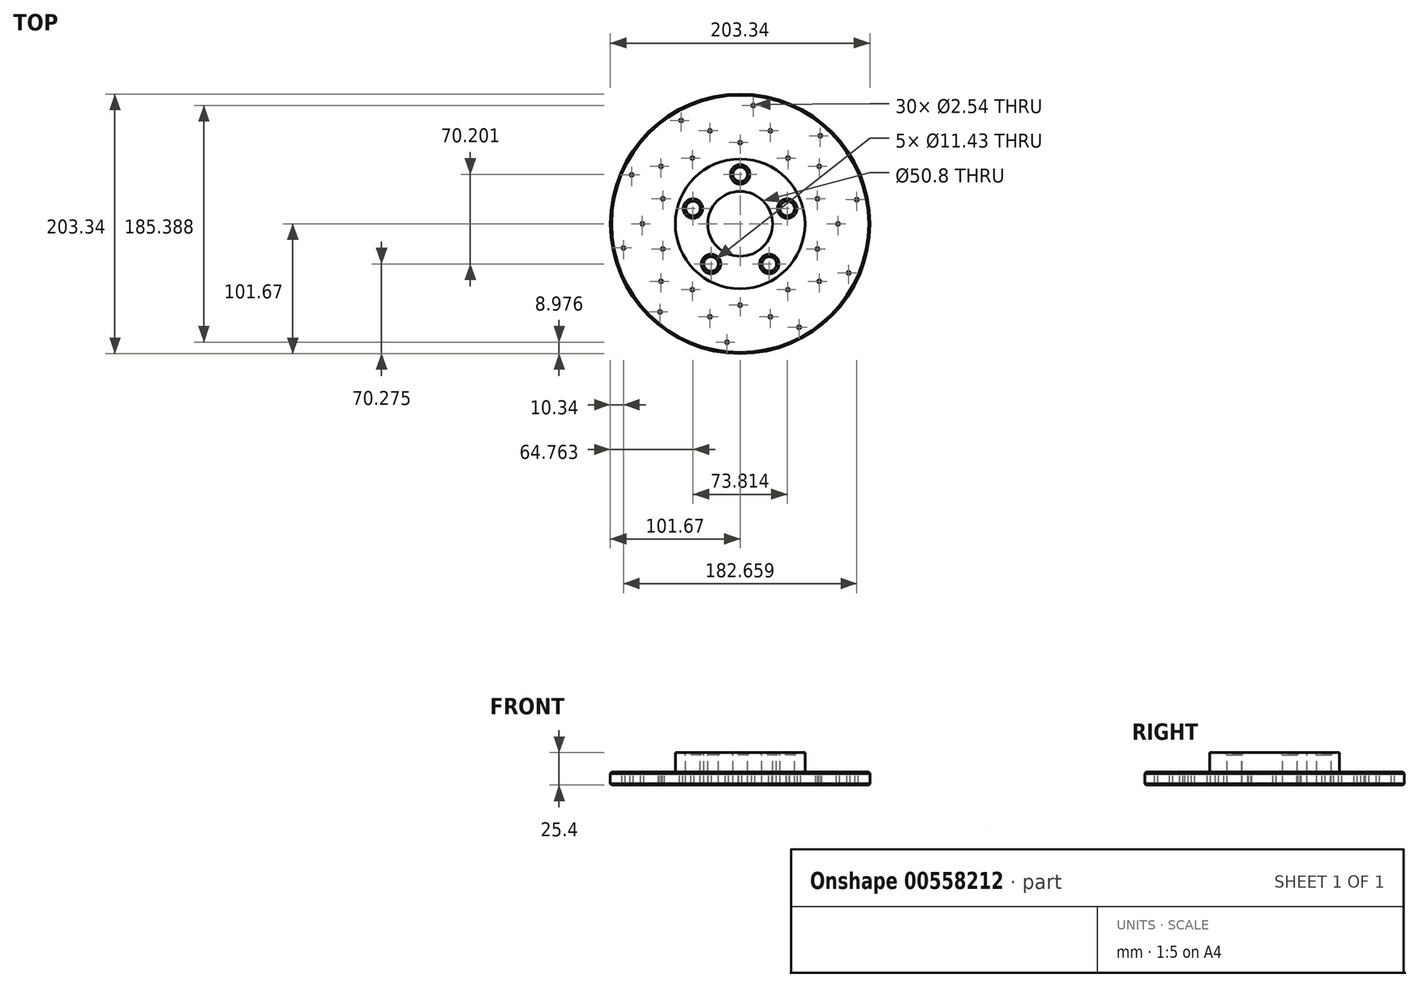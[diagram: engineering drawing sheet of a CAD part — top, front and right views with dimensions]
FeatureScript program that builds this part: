
annotation { "Feature Type Name" : "Feature", "Feature Type Description" : "" }
export const myFeature = defineFeature(function(context is Context, id is Id, definition is map)
    precondition{}
    {
        {
            var Q0;
            Q0=qCreatedBy(makeId("Top.planeOp"),FACE);
            var sketch = newSketch(context, id + "F0", { "sketchPlane" : qUnion([Q0])});
            skCircle(sketch, "E0", {"center": v(0, 0) * mm, "radius": 101.67 * mm});
            skSolve(sketch);
        }
        {
            var Q0;
            Q0=makeQuery(id+"F0.imprint","IMPRINT",FACE,{"disambiguationData":[TD([[makeQuery(id+"F0.imprint","IMPRINT",EDGE,{"derivedFrom":sQuery(id+"F0.wireOp",EDGE,"E0")}),1.0]])]});
            extrude(context, id + "F1", {"entities" : qUnion([Q0]), "depth" : 10.16 * mm, "offsetDistance" : 25.4 * mm});
        }
        {
            var Q0;
            Q0=makeQuery(id+"F1.opExtrude","CAP_FACE",FACE,{"disambiguationData":[OSD([sQuery(id+"F0.wireOp",EDGE,"E0")])],"isStart":false});
            var sketch = newSketch(context, id + "F2", { "sketchPlane" : qUnion([Q0])});
            skCircle(sketch, "E1", {"center": v(0, 0) * mm, "radius": 50.83 * mm});
            skSolve(sketch);
        }
        {
            var Q0;
            Q0=makeQuery(id+"F2.imprint","IMPRINT",FACE,{"disambiguationData":[TD([[makeQuery(id+"F2.imprint","IMPRINT",EDGE,{"derivedFrom":sQuery(id+"F2.wireOp",EDGE,"E1")}),1.0]])]});
            var Q1;
            Q1=sQuery(id+"F2.wireOp",EDGE,"E1");
            extrude(context, id + "F3", {"entities" : qUnion([Q0]), "operationType" : NewBodyOperationType.ADD, "surfaceEntities" : qUnion([Q1]), "depth" : 15.24 * mm, "offsetDistance" : 25.4 * mm});
        }
        {
            var Q0;
            Q0=makeQuery(id+"F3.opExtrude","CAP_FACE",FACE,{"disambiguationData":[OSD([sQuery(id+"F2.wireOp",EDGE,"E1")])],"isStart":false});
            var sketch = newSketch(context, id + "F4", { "sketchPlane" : qUnion([Q0])});
            skPoint(sketch, "E2", {"position": v(0, 0) * mm});
            skSolve(sketch);
        }
        {
            var Q0;
            Q0=sQuery(id+"F4.wireOp",VERTEX,"E2");
            var Q1;
            Q1=makeQuery(id+"F1.opExtrude","SWEPT_BODY",BODY,{"disambiguationData":[OSD([sQuery(id+"F0.wireOp",EDGE,"E0")])]});
            hole(context, id + "F5", {"style" : HoleStyle.SIMPLE, "endStyle" : HoleEndStyle.THROUGH, "holeDiameter" : 50.8 * mm, "isTappedThrough" : true, "tappedDepth" : 12.7 * mm, "tapClearance" : 3, "locations" : qUnion([Q0]), "scope" : qUnion([Q1])});
        }
        {
            var Q0;
            Q0=makeQuery(id+"F3.opExtrude","CAP_FACE",FACE,{"disambiguationData":[OSD([sQuery(id+"F2.wireOp",EDGE,"E1")])],"isStart":false});
            var sketch = newSketch(context, id + "F6", { "sketchPlane" : qUnion([Q0])});
            skCircle(sketch, "E3.cCircle", {"center": v(0, 0) * mm, "radius": 38.8 * mm, "construction": true});
            skLineSegment(sketch, "E3.0", {"start": v(0, 38.8) * mm, "end": v(36.9, 12) * mm});
            skLineSegment(sketch, "E3.1", {"start": v(36.9, 12) * mm, "end": v(22.8, -31.4) * mm});
            skLineSegment(sketch, "E3.2", {"start": v(22.8, -31.4) * mm, "end": v(-22.8, -31.4) * mm});
            skLineSegment(sketch, "E3.3", {"start": v(-22.8, -31.4) * mm, "end": v(-36.9, 12) * mm});
            skLineSegment(sketch, "E3.4", {"start": v(-36.9, 12) * mm, "end": v(0, 38.8) * mm});
            skPoint(sketch, "E4", {"position": v(0, 38.8) * mm});
            skPoint(sketch, "E5", {"position": v(-36.9, 12) * mm});
            skPoint(sketch, "E6", {"position": v(-22.8, -31.4) * mm});
            skPoint(sketch, "E7", {"position": v(22.8, -31.4) * mm});
            skPoint(sketch, "E8", {"position": v(36.9, 12) * mm});
            skSolve(sketch);
        }
        {
            var Q0;
            Q0=sQuery(id+"F6.wireOp",VERTEX,"E4");
            var Q1;
            Q1=sQuery(id+"F6.wireOp",VERTEX,"E5");
            var Q2;
            Q2=sQuery(id+"F6.wireOp",VERTEX,"E6");
            var Q3;
            Q3=sQuery(id+"F6.wireOp",VERTEX,"E7");
            var Q4;
            Q4=sQuery(id+"F6.wireOp",VERTEX,"E8");
            var Q5;
            Q5=makeQuery(id+"F1.opExtrude","SWEPT_BODY",BODY,{"disambiguationData":[OSD([sQuery(id+"F0.wireOp",EDGE,"E0")])]});
            hole(context, id + "F7", {"style" : HoleStyle.C_SINK, "endStyle" : HoleEndStyle.THROUGH, "holeDiameter" : 11.43 * mm, "cSinkDiameter" : 15.24 * mm, "cSinkAngle" : 90 * degree, "isTappedThrough" : true, "tappedDepth" : 12.7 * mm, "tapClearance" : 3, "locations" : qUnion([Q0, Q1, Q2, Q3, Q4]), "scope" : qUnion([Q5])});
        }
        {
            var Q0;
            Q0=makeQuery(id+"F1.opExtrude","CAP_FACE",FACE,{"disambiguationData":[OSD([sQuery(id+"F0.wireOp",EDGE,"E0")])],"isStart":false});
            var sketch = newSketch(context, id + "F8", { "sketchPlane" : qUnion([Q0])});
            skCircle(sketch, "E9.cCircle", {"center": v(0, 0) * mm, "radius": 72.85 * mm, "construction": true});
            skLineSegment(sketch, "E9.0", {"start": v(-23.67, 72.85) * mm, "end": v(23.67, 72.85) * mm});
            skLineSegment(sketch, "E9.1", {"start": v(23.67, 72.85) * mm, "end": v(61.97, 45.02) * mm});
            skLineSegment(sketch, "E9.2", {"start": v(61.97, 45.02) * mm, "end": v(76.6, 0) * mm});
            skLineSegment(sketch, "E9.3", {"start": v(76.6, 0) * mm, "end": v(61.97, -45.02) * mm});
            skLineSegment(sketch, "E9.4", {"start": v(61.97, -45.02) * mm, "end": v(23.67, -72.85) * mm});
            skLineSegment(sketch, "E9.5", {"start": v(23.67, -72.85) * mm, "end": v(-23.67, -72.85) * mm});
            skLineSegment(sketch, "E9.6", {"start": v(-23.67, -72.85) * mm, "end": v(-61.97, -45.02) * mm});
            skLineSegment(sketch, "E9.7", {"start": v(-61.97, -45.02) * mm, "end": v(-76.6, 0) * mm});
            skLineSegment(sketch, "E9.8", {"start": v(-76.6, 0) * mm, "end": v(-61.97, 45.02) * mm});
            skLineSegment(sketch, "E9.9", {"start": v(-61.97, 45.02) * mm, "end": v(-23.67, 72.85) * mm});
            skPoint(sketch, "E9.0.midPoint", {"position": v(0, 72.85) * mm});
            skCircle(sketch, "E10.cCircle", {"center": v(0, 0) * mm, "radius": 88.7 * mm, "construction": true});
            skLineSegment(sketch, "E10.0", {"start": v(-46.18, 81.03) * mm, "end": v(10.27, 92.7) * mm});
            skLineSegment(sketch, "E10.1", {"start": v(10.27, 92.7) * mm, "end": v(62.79, 68.96) * mm});
            skLineSegment(sketch, "E10.2", {"start": v(62.79, 68.96) * mm, "end": v(91.33, 18.88) * mm});
            skLineSegment(sketch, "E10.3", {"start": v(91.33, 18.88) * mm, "end": v(84.98, -38.4) * mm});
            skLineSegment(sketch, "E10.4", {"start": v(84.98, -38.4) * mm, "end": v(46.18, -81.03) * mm});
            skLineSegment(sketch, "E10.5", {"start": v(46.18, -81.03) * mm, "end": v(-10.27, -92.7) * mm});
            skLineSegment(sketch, "E10.6", {"start": v(-10.27, -92.7) * mm, "end": v(-62.79, -68.96) * mm});
            skLineSegment(sketch, "E10.7", {"start": v(-62.79, -68.96) * mm, "end": v(-91.33, -18.88) * mm});
            skLineSegment(sketch, "E10.8", {"start": v(-91.33, -18.88) * mm, "end": v(-84.98, 38.4) * mm});
            skLineSegment(sketch, "E10.9", {"start": v(-84.98, 38.4) * mm, "end": v(-46.18, 81.03) * mm});
            skPoint(sketch, "E10.0.midPoint", {"position": v(-17.96, 86.86) * mm});
            skCircle(sketch, "E11.cCircle", {"center": v(0, 0) * mm, "radius": 60.55 * mm, "construction": true});
            skLineSegment(sketch, "E11.0", {"start": v(0.03, 63.67) * mm, "end": v(37.45, 51.49) * mm});
            skLineSegment(sketch, "E11.1", {"start": v(37.45, 51.49) * mm, "end": v(60.56, 19.64) * mm});
            skLineSegment(sketch, "E11.2", {"start": v(60.56, 19.64) * mm, "end": v(60.54, -19.7) * mm});
            skLineSegment(sketch, "E11.3", {"start": v(60.54, -19.7) * mm, "end": v(37.4, -51.53) * mm});
            skLineSegment(sketch, "E11.4", {"start": v(37.4, -51.53) * mm, "end": v(-0.03, -63.67) * mm});
            skLineSegment(sketch, "E11.5", {"start": v(-0.03, -63.67) * mm, "end": v(-37.45, -51.49) * mm});
            skLineSegment(sketch, "E11.6", {"start": v(-37.45, -51.49) * mm, "end": v(-60.56, -19.64) * mm});
            skLineSegment(sketch, "E11.7", {"start": v(-60.56, -19.64) * mm, "end": v(-60.54, 19.7) * mm});
            skLineSegment(sketch, "E11.8", {"start": v(-60.54, 19.7) * mm, "end": v(-37.4, 51.53) * mm});
            skLineSegment(sketch, "E11.9", {"start": v(-37.4, 51.53) * mm, "end": v(0.03, 63.67) * mm});
            skPoint(sketch, "E11.0.midPoint", {"position": v(18.74, 57.58) * mm});
            skPoint(sketch, "E12", {"position": v(10.27, 92.7) * mm});
            skPoint(sketch, "E13", {"position": v(23.67, 72.85) * mm});
            skPoint(sketch, "E14", {"position": v(37.45, 51.49) * mm});
            skPoint(sketch, "E15", {"position": v(0.03, 63.67) * mm});
            skPoint(sketch, "E16", {"position": v(-23.67, 72.85) * mm});
            skPoint(sketch, "E17", {"position": v(-46.18, 81.03) * mm});
            skPoint(sketch, "E18", {"position": v(-37.4, 51.53) * mm});
            skPoint(sketch, "E19", {"position": v(-61.97, 45.02) * mm});
            skPoint(sketch, "E20", {"position": v(-84.98, 38.4) * mm});
            skPoint(sketch, "E21", {"position": v(-60.54, 19.7) * mm});
            skPoint(sketch, "E22", {"position": v(-76.6, 0) * mm});
            skPoint(sketch, "E23", {"position": v(-91.33, -18.88) * mm});
            skPoint(sketch, "E24", {"position": v(-62.79, -68.96) * mm});
            skPoint(sketch, "E25", {"position": v(-61.97, -45.02) * mm});
            skPoint(sketch, "E26", {"position": v(-60.56, -19.64) * mm});
            skPoint(sketch, "E27", {"position": v(-37.45, -51.49) * mm});
            skPoint(sketch, "E28", {"position": v(-23.67, -72.85) * mm});
            skPoint(sketch, "E29", {"position": v(-10.27, -92.7) * mm});
            skPoint(sketch, "E30", {"position": v(-0.03, -63.67) * mm});
            skPoint(sketch, "E31", {"position": v(23.67, -72.85) * mm});
            skPoint(sketch, "E32", {"position": v(46.18, -81.03) * mm});
            skPoint(sketch, "E33", {"position": v(37.4, -51.53) * mm});
            skPoint(sketch, "E34", {"position": v(61.97, -45.02) * mm});
            skPoint(sketch, "E35", {"position": v(84.98, -38.4) * mm});
            skPoint(sketch, "E36", {"position": v(60.54, -19.7) * mm});
            skPoint(sketch, "E37", {"position": v(76.6, 0) * mm});
            skPoint(sketch, "E38", {"position": v(91.33, 18.88) * mm});
            skPoint(sketch, "E39", {"position": v(60.56, 19.64) * mm});
            skPoint(sketch, "E40", {"position": v(61.97, 45.02) * mm});
            skPoint(sketch, "E41", {"position": v(62.79, 68.96) * mm});
            skSolve(sketch);
        }
        {
            var Q0;
            Q0=sQuery(id+"F8.wireOp",VERTEX,"E12");
            var Q1;
            Q1=sQuery(id+"F8.wireOp",VERTEX,"E17");
            var Q2;
            Q2=sQuery(id+"F8.wireOp",VERTEX,"E16");
            var Q3;
            Q3=sQuery(id+"F8.wireOp",VERTEX,"E15");
            var Q4;
            Q4=sQuery(id+"F8.wireOp",VERTEX,"E13");
            var Q5;
            Q5=sQuery(id+"F8.wireOp",VERTEX,"E14");
            var Q6;
            Q6=sQuery(id+"F8.wireOp",VERTEX,"E41");
            var Q7;
            Q7=sQuery(id+"F8.wireOp",VERTEX,"E40");
            var Q8;
            Q8=sQuery(id+"F8.wireOp",VERTEX,"E39");
            var Q9;
            Q9=sQuery(id+"F8.wireOp",VERTEX,"E38");
            var Q10;
            Q10=sQuery(id+"F8.wireOp",VERTEX,"E37");
            var Q11;
            Q11=sQuery(id+"F8.wireOp",VERTEX,"E36");
            var Q12;
            Q12=sQuery(id+"F8.wireOp",VERTEX,"E35");
            var Q13;
            Q13=sQuery(id+"F8.wireOp",VERTEX,"E34");
            var Q14;
            Q14=sQuery(id+"F8.wireOp",VERTEX,"E33");
            var Q15;
            Q15=sQuery(id+"F8.wireOp",VERTEX,"E32");
            var Q16;
            Q16=sQuery(id+"F8.wireOp",VERTEX,"E31");
            var Q17;
            Q17=sQuery(id+"F8.wireOp",VERTEX,"E30");
            var Q18;
            Q18=sQuery(id+"F8.wireOp",VERTEX,"E29");
            var Q19;
            Q19=sQuery(id+"F8.wireOp",VERTEX,"E28");
            var Q20;
            Q20=sQuery(id+"F8.wireOp",VERTEX,"E27");
            var Q21;
            Q21=sQuery(id+"F8.wireOp",VERTEX,"E24");
            var Q22;
            Q22=sQuery(id+"F8.wireOp",VERTEX,"E25");
            var Q23;
            Q23=sQuery(id+"F8.wireOp",VERTEX,"E26");
            var Q24;
            Q24=sQuery(id+"F8.wireOp",VERTEX,"E23");
            var Q25;
            Q25=sQuery(id+"F8.wireOp",VERTEX,"E22");
            var Q26;
            Q26=sQuery(id+"F8.wireOp",VERTEX,"E21");
            var Q27;
            Q27=sQuery(id+"F8.wireOp",VERTEX,"E20");
            var Q28;
            Q28=sQuery(id+"F8.wireOp",VERTEX,"E19");
            var Q29;
            Q29=sQuery(id+"F8.wireOp",VERTEX,"E18");
            var Q30;
            Q30=makeQuery(id+"F1.opExtrude","SWEPT_BODY",BODY,{"disambiguationData":[OSD([sQuery(id+"F0.wireOp",EDGE,"E0")])]});
            hole(context, id + "F9", {"style" : HoleStyle.SIMPLE, "endStyle" : HoleEndStyle.THROUGH, "holeDiameter" : 2.54 * mm, "isTappedThrough" : true, "tappedDepth" : 12.7 * mm, "tapClearance" : 3, "locations" : qUnion([Q0, Q1, Q2, Q3, Q4, Q5, Q6, Q7, Q8, Q9, Q10, Q11, Q12, Q13, Q14, Q15, Q16, Q17, Q18, Q19, Q20, Q21, Q22, Q23, Q24, Q25, Q26, Q27, Q28, Q29]), "scope" : qUnion([Q30])});
        }
        {
            var Q0;
            Q0=makeQuery(id+"F1.opExtrude","SWEPT_FACE",FACE,{"disambiguationData":[OSD([sQuery(id+"F0.wireOp",EDGE,"E0")])]});
            chamfer(context, id + "F10", {"entities" : qUnion([Q0]), "width" : 1.02 * mm, "tangentPropagation" : true});
        }
    });
